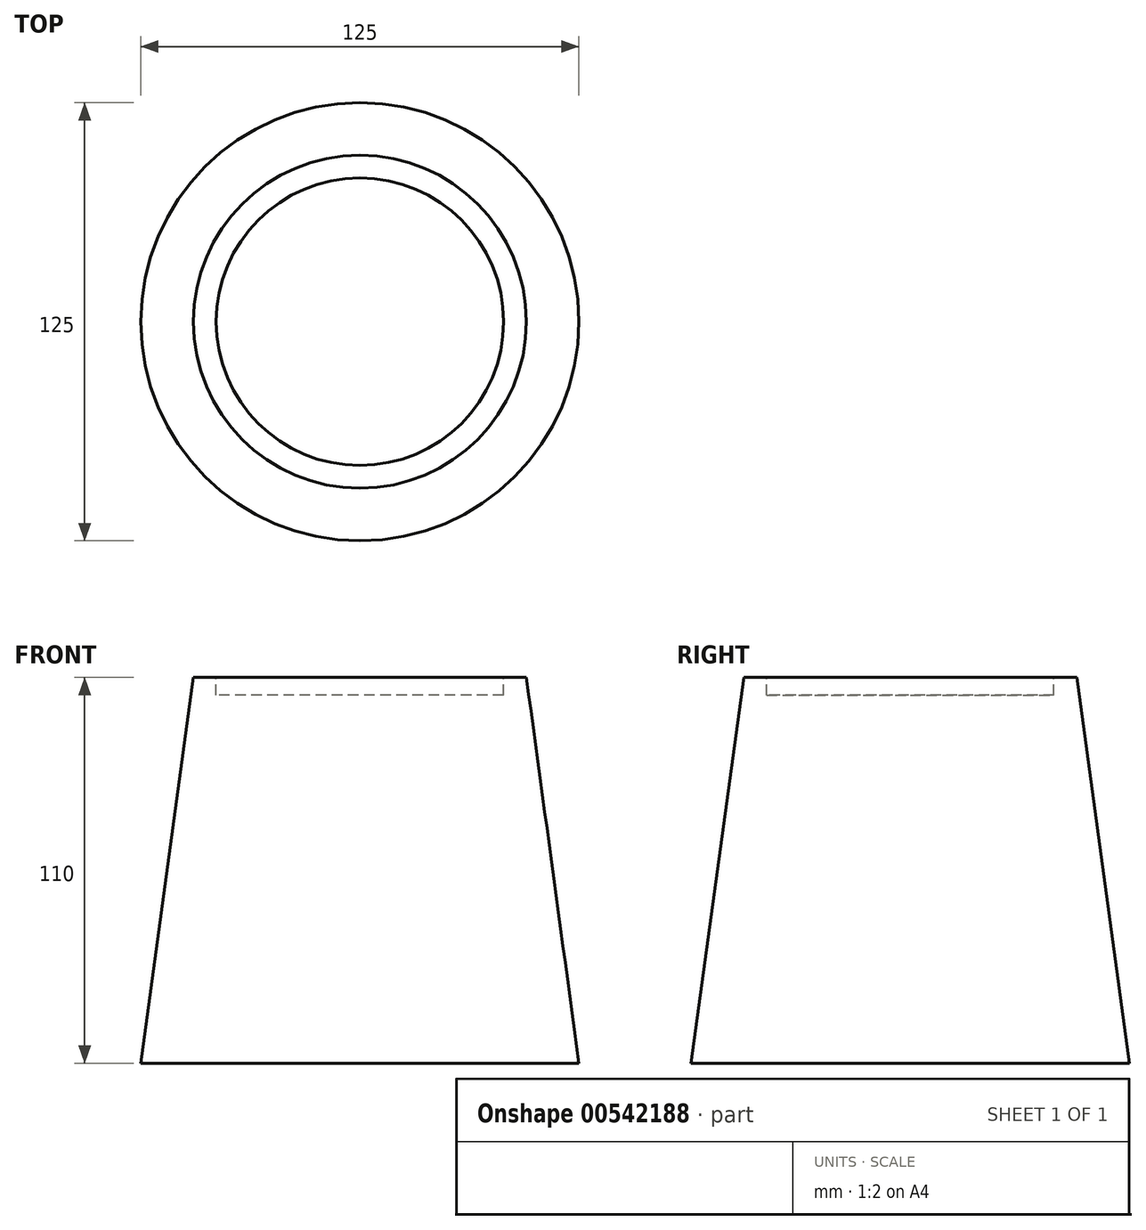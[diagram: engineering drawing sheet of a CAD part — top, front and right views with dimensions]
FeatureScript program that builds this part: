
annotation { "Feature Type Name" : "Feature", "Feature Type Description" : "" }
export const myFeature = defineFeature(function(context is Context, id is Id, definition is map)
    precondition{}
    {
        {
            var Q0;
            Q0=qCreatedBy(makeId("Top.planeOp"),FACE);
            var sketch = newSketch(context, id + "F0", { "sketchPlane" : qUnion([Q0])});
            skCircle(sketch, "E0", {"center": v(0, 0) * mm, "radius": 62.5 * mm});
            skSolve(sketch);
        }
        {
            var Q0;
            Q0=makeQuery(id+"F0.imprint","IMPRINT",FACE,{"disambiguationData":[TD([[makeQuery(id+"F0.imprint","IMPRINT",EDGE,{"derivedFrom":sQuery(id+"F0.wireOp",EDGE,"E0")}),1.0]])]});
            extrude(context, id + "F1", {"entities" : qUnion([Q0]), "depth" : 110 * mm, "offsetDistance" : 25 * mm});
        }
        {
            var Q0;
            Q0=makeQuery(id+"F1.opExtrude","CAP_EDGE",EDGE,{"disambiguationData":[OSD([sQuery(id+"F0.wireOp",EDGE,"E0")])],"isStart":false});
            chamfer(context, id + "F2", {"entities" : qUnion([Q0]), "chamferType" : ChamferType.TWO_OFFSETS, "width1" : 15 * mm, "oppositeDirection" : false, "width2" : 110 * mm, "tangentPropagation" : true});
        }
        {
            var Q0;
            Q0=makeQuery(id+"F1.opExtrude","CAP_FACE",FACE,{"disambiguationData":[OSD([sQuery(id+"F0.wireOp",EDGE,"E0")])],"isStart":false});
            var sketch = newSketch(context, id + "F3", { "sketchPlane" : qUnion([Q0])});
            skCircle(sketch, "E1", {"center": v(0, 0) * mm, "radius": 41 * mm});
            skSolve(sketch);
        }
        {
            var Q0;
            Q0=makeQuery(id+"F3.imprint","IMPRINT",FACE,{"disambiguationData":[TD([[makeQuery(id+"F3.imprint","IMPRINT",EDGE,{"derivedFrom":sQuery(id+"F3.wireOp",EDGE,"E1")}),1.0]])]});
            extrude(context, id + "F4", {"entities" : qUnion([Q0]), "operationType" : NewBodyOperationType.REMOVE, "oppositeDirection" : true, "depth" : 5 * mm, "offsetDistance" : 25 * mm});
        }
    });
